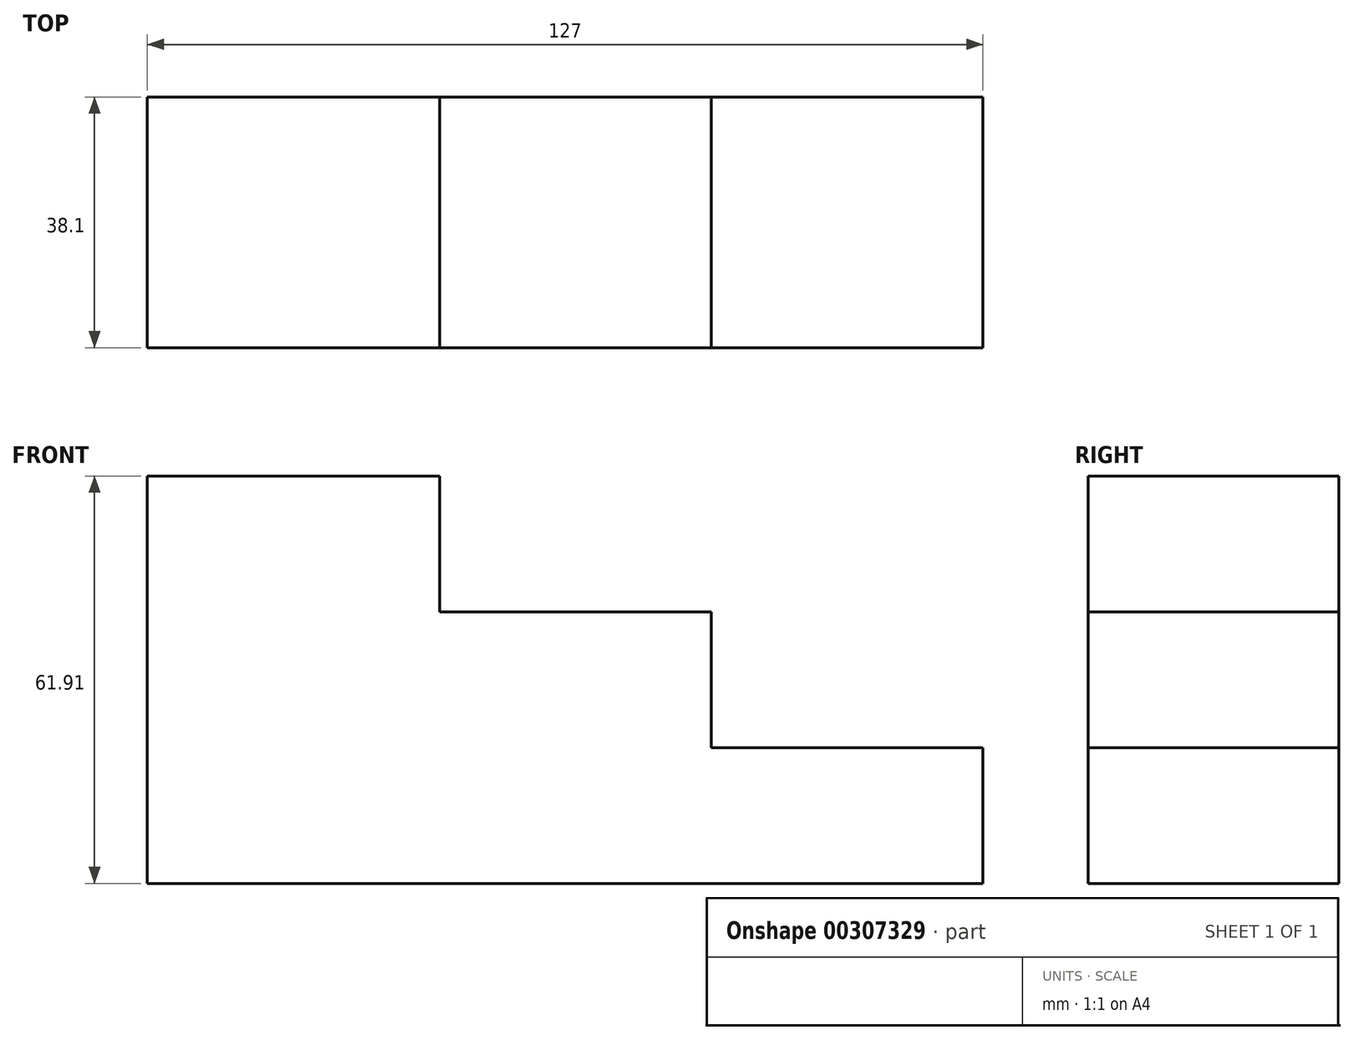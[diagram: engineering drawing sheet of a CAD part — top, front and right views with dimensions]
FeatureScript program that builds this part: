
annotation { "Feature Type Name" : "Feature", "Feature Type Description" : "" }
export const myFeature = defineFeature(function(context is Context, id is Id, definition is map)
    precondition{}
    {
        {
            var Q0;
            Q0=qCreatedBy(makeId("Front.planeOp"),FACE);
            var sketch = newSketch(context, id + "F0", { "sketchPlane" : qUnion([Q0])});
            skLineSegment(sketch, "E0", {"start": v(-67.4, -15) * mm, "end": v(59.6, -15) * mm});
            skLineSegment(sketch, "E1", {"start": v(-22.95, 46.91) * mm, "end": v(-22.95, 26.27) * mm});
            skLineSegment(sketch, "E2", {"start": v(-22.95, 26.27) * mm, "end": v(18.32, 26.27) * mm});
            skLineSegment(sketch, "E3", {"start": v(18.32, 26.27) * mm, "end": v(18.32, 5.64) * mm});
            skLineSegment(sketch, "E4", {"start": v(18.32, 5.64) * mm, "end": v(59.6, 5.64) * mm});
            skLineSegment(sketch, "E5", {"start": v(59.6, 5.64) * mm, "end": v(59.6, -15) * mm});
            skLineSegment(sketch, "E6", {"start": v(-67.4, -15) * mm, "end": v(-67.4, 46.91) * mm});
            skLineSegment(sketch, "E7", {"start": v(-22.95, 46.91) * mm, "end": v(-67.4, 46.91) * mm});
            skSolve(sketch);
        }
        {
            var Q0;
            Q0=makeQuery(id+"F0.imprint","IMPRINT",FACE,{"disambiguationData":[TD([[makeQuery(id+"F0.imprint","IMPRINT",EDGE,{"derivedFrom":sQuery(id+"F0.wireOp",EDGE,"E0")}),1.0]])]});
            extrude(context, id + "F1", {"entities" : qUnion([Q0]), "depth" : 38.1 * mm});
        }
    });
